# Revit family: URA_Eclairage_de_Securite_URALIFE V_NOIR_LSC – pose Murale
name_source: partatom
category: Luminaires
units: mm (PartAtom-declared; Revit-internal decimal feet)

## family parameters
Cote de connecteur circulaire = Utiliser le diamètre
Couper avec des vides une fois chargée = Non
Hôte = Face
Numéro OmniClass = 23.80.70.11.21
Partagée = Non
Repere pour localisation dans la piece = Non
Source d'éclairage = Non
Titre OmniClass = Emergency Lighting
Type d'élément = Normal

## types (5) — shared parameters
Alimentation de secours = Centralisé (source centrale)
Classe de protection = II
Conditions Générale d'Utilisation = https://export.legrand.com
Couleur = Noir
Elévation par défaut = 2300 mm
Fabricant = URA
Fréquence = 50-60
IK = 07
IP = 43
Matière = Plastique
Objet Connecté = Oui
Percement = 250 mm  [stored 0.82021 ft]
Système de contrôle = sans
Temperature d'utilisation MIN-MAX = 0-35
Tension = 48-230 AC/DC
Type de commutation = Non permanent
Type de connexion = autre
URL = www.ura.fr
Visibilité AMB Encastré horizontale = Non
Visibilité EVAC Saillie horizontale = Non
capacité des bornes = 1.5
source lumineuse = LED non interchangeable
zero-valued in all types: Entraxe de fixation verticale

## per-type parameters (varying)
| type | Consommation en veille | Désignation produit | Entraxe de fixation horizontale | Flux lumineux utile | Fonction | Hauteur | Hauteur encastrement | Largeur | Largeur encastrement | Longueur | Longueur d'encastrement | Mode de pose | Picto AMB | Picto EVAC | Puissance du système | Référence / Modèle | Type de pictogramme | Visibilité AMB Equerre | Visibilité AMB Saillie horizontale | Visibilité EVAC Equerre | Visibilité EVAC Saillie horizontale rect | Visibilité EVAC Saillie verticale |
| .1-LSC Evacuation 48-230V pose murale en applique (noir) | 6.5 mA | LSC URALIFE V NOIR, EVACUATION, 48-220VDC / 230VAC, POSE MURALE SAILLIE | 90-100 | 0 lm | Éclairage d'évacuation | 38 mm  [stored 0.124672 ft] | 0 mm  [stored 0 ft] | 106 mm  [stored 0.347769 ft] | 0 mm  [stored 0 ft] | 206 mm  [stored 0.675853 ft] | 0 mm  [stored 0 ft] | Montage en saillie (mur) | Non | Oui | 2 W | UR-128314V | Feuillet/plaque inséré(e) | Non | Non | Non | Oui | Non |
| .2-LSC Evacuation 48-230V pose murale en drapeau avec equerre (noir) | 6.5 mA | LSC URALIFE V NOIR, EVACUATION, 48-220VDC / 230VAC, POSE PLAFOND ENCASTREE OU SAILLIE | 184-188 | 45 lm | Éclairage d'évacuation | 138 mm  [stored 0.452756 ft] | 55 mm  [stored 0.180446 ft] | 62 mm  [stored 0.203412 ft] | 70 mm  [stored 0.229659 ft] | 219 mm  [stored 0.718504 ft] | 245 mm  [stored 0.803806 ft] | En saillie et encastré | Non | Oui | 2 W | UR-128414V | Feuillet/plaque inséré(e) | Non | Non | Oui | Non | Non |
| .3-LSC Evacuation 48-230V pose murale verticale en saillie (noir) | 6.5 mA | LSC URALIFE V NOIR, EVACUATION, 48-220VDC / 230VAC, POSE PLAFOND ENCASTREE OU SAILLIE | 184-188 | 45 lm | Éclairage d'évacuation | 138 mm  [stored 0.452756 ft] | 55 mm  [stored 0.180446 ft] | 62 mm  [stored 0.203412 ft] | 70 mm  [stored 0.229659 ft] | 219 mm  [stored 0.718504 ft] | 245 mm  [stored 0.803806 ft] | En saillie et encastré | Non | Oui | 2 W | UR-128414V | Feuillet/plaque inséré(e) | Non | Non | Non | Non | Oui |
| .4-LSC Ambiance 48-230V pose murale en saillie (noir) | 22.0 mA | LSC URALIFE V NOIR, AMBIANCE, 48-220VDC / 230VAC, POSE PLAFOND ENCASTREE OU SAILLIE | 184-188 | 400 lm | Éclairage d'ambiance (anti-panique) | 36 mm  [stored 0.11811 ft] | 55 mm  [stored 0.180446 ft] | 62 mm  [stored 0.203412 ft] | 70 mm  [stored 0.229659 ft] | 219 mm  [stored 0.718504 ft] | 245 mm  [stored 0.803806 ft] | En saillie et encastré | Oui | Non | 5 W | UR-128424V |  | Non | Oui | Non | Non | Non |
| .5-LSC Ambiance 48-230V pose murale en drapeau avec equerre (noir) | 22.0 mA | LSC URALIFE V NOIR, AMBIANCE, 48-220VDC / 230VAC, POSE PLAFOND ENCASTREE OU SAILLIE | 184-188 | 400 lm | Éclairage d'ambiance (anti-panique) | 36 mm  [stored 0.11811 ft] | 55 mm  [stored 0.180446 ft] | 62 mm  [stored 0.203412 ft] | 70 mm  [stored 0.229659 ft] | 219 mm  [stored 0.718504 ft] | 245 mm  [stored 0.803806 ft] | En saillie et encastré | Oui | Non | 5 W | UR-128424V |  | Oui | Non | Non | Non | Non |

note: [stored X ft] marks values corroborated as IEEE doubles in the binary element streams (Revit-internal decimal feet)
